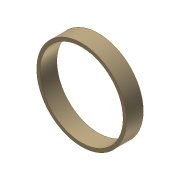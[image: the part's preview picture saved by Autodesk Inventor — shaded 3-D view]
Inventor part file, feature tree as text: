
AUTODESK INVENTOR PART (.ipt)
format: ipt  version: 2012 (Build 160160000, 160)  size: 80,896 bytes
history: native  units: in
note: dims shown in document units (in); Inventor stores cm internally (conversion verified against a paired STEP export)
features: extrude x1, sketch x1
ambient origin geometry x8: Origin, YZ Plane, XZ Plane, XY Plane, X Axis, Y Axis, Z Axis, Center Point
bodies: Solid1 (feature_tree)
feature tree (2):
  extrude  "Extrusion1"  Depth=0.3in
  sketch  "Sketch1"  dims[d0=7.4in d1=0.3in d2=1.5in d3=0.0in]
